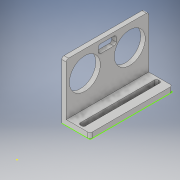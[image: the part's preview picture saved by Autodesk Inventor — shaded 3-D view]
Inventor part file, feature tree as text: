
AUTODESK INVENTOR PART (.ipt)
format: ipt  version: 2019 (Build 230136000, 136)  size: 173,056 bytes
history: native  units: in
note: dims shown in document units (in); Inventor stores cm internally (conversion verified against a paired STEP export)
features: extrude x4, sketch x2, fillet x2, imported_body x1, hole x1, other x1
ambient origin geometry x8: Origin, YZ Plane, XZ Plane, XY Plane, X Axis, Y Axis, Z Axis, Center Point
bodies: Solid1 (feature_tree)
feature tree (11):
  imported_body  "Base"
  extrude  "Extrusion1"  Depth=1.16in TaperAngle=0.0deg
  extrude  "Extrusion2"  Depth=1.16in TaperAngle=0.0deg
  sketch  "Sketch5"  dims[d4=0.1181in d5=0.0in d7=1.16in d8=0.0in]
  hole  "Hole2"  [1 undecoded]
  extrude  "Extrusion4"  Depth=0.05in
  fillet  "Fillet1"  Radius=0.1181in
  fillet  "Fillet2"  Radius=0.04in
  extrude  "Extrusion6"  Depth=0.04in TaperAngle=0.0deg
  other  "FrontWall"
  sketch  "Sketch8"  dims[d27=1.887in d28=1.7894in d30=0.689in d31=0.75in d32=0.375in d33=0.25in d34=0.5635in d35=1.0in d36=0.8108in d37=1.16in d38=0.0in d60=0.05in d61=0.05in d62=0.1181in d63=0.04in d64=1.0in d65=0.0in]
note: 1 required parameter value undecoded (feature->parameter linkage not recoverable at this tier; creation-order binding heuristic only, values carry confidence <= 0.55)
